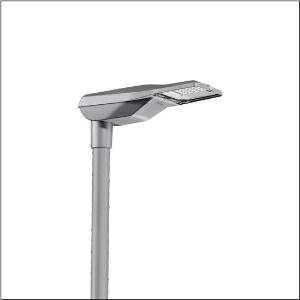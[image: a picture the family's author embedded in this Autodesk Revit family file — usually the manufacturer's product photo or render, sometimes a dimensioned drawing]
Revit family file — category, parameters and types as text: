
# Revit family: streetlight_sl_21_iq_micro___st1_0a_5xe1d41d08cb_ed56
name_source: partatom
category: Lighting Fixtures
units: mm (PartAtom-declared; Revit-internal decimal feet)

## family parameters
Cut with Voids When Loaded = No
Host = Face
Light Source = No
Part Type = Normal
Room Calculation Point = No
Round Connector Dimension = Use Diameter
Shared = No

## types (1)
- --- (1 x LED, 2980 lm, 19.4 W, 4000K)
    Apparent Load = 19 VA
    CIE Flux Codes = 37 72 97 100 100
    Color Rendering = 70
    Color Temperature = 4000K
    Default Elevation = 1800 mm
    Description = Streetlight SL 21 iQ micro, mast luminaire, primary light control with lens, of PMMA, primary optical cover: cover, of toughened safety glass, transparent, light distribution: ST1.0a, light emission: direct distribution, primary light characteristic: asymmetric, installation type: post-top, side-entry, LED, High Power LED, rated luminous flux: 2.980lm, luminous efficacy: 154lm/W, light colour: 740, colour temperature: 4000K, control gear: iQ-Comfort, control: Auto-Match, Temp-Guard, Lumen-Switch, Night-Set, Smart-Wire, Light-Fading, Desk-Remote (wireless, voltage-free reading and setting of iQ features in the workshop via application-optimized NFC function/RFID function), optimised constant luminous flux control (CLO 2.0), pre-setting: linear dimming characteristic, mains connection: 220..240V, AC, 50/60Hz, start of lifetime: 19W, end of service life: 20W, reduction: 10W, luminaire housing, of diecast aluminium, powder-coated, SITECO metallic grey (DB 702S), corrosivity category C5 high according to DIN EN ISO 12944, please order mast flange separately, inclination adjustable: 0°, 5°, 10°, 15°, sealing non-destructively replaceable, multi-level sealing system, length: 528mm, width: 235mm, height: 110mm, mast flange for spigot size: 42mm (side-entry): 5XC10008XM4, 60/48mm (side-entry/post-top): 5XC10108XM2, 76/60mm (side-entry/post-top): 5XC10108XM1, protection rating (complete): IP66, insulation class (complete): insulation class II (safety insulation), certification: CE, ENEC, ENEC+, VDE, impact resistance: IK10, permissible operating ambient temperature for outdoor applications: -40..+50°C, standard-compliant lighting for roads and squares, packaging unit: 1 piece

Light Distribution: ST1.0a
    Height = 110 mm
    Lamp = 1 x LED
    Lamp Light Flux = 2980 lm
    Lamp Power = 19.4 W
    Lamp count = 1
    Length = 528 mm
    Luminous efficacy = 154 lm/W
    Manufacturer = Siteco
    ModVariant = No
    Model = 5XE1D41D08CB
    Mounting Place = Pole
    Mounting Type = Pole top
    Number of Poles = 1
    OnlyDefault = Yes
    Power Factor = 1
    Product Name = Streetlight SL 21 iQ micro | ST1.0a
    Product group = mast luminaire | pylon top
    ProductGroupID = 6100
    Protection Class = Protection class II
    Protection Degree = IP 66
    RLX_Detail_Level = 1
    RLX_Emergency_Light_Flux = 0 lm
    RLX_Emergency_Type = 0
    RLX_Emergency_Type_DB = No
    RlxData = <blob elided: 98889 chars, md5=e276a93e>
    Socket = socket
    Standby Power = 0 W
    System Light Flux = 2980 lm
    System Power = 19 W
    Type Comments = factory setting: luminous flux: 100 % | dim-lin: 254 | 387 mA
    Type Image = l_1006881.jpg
    URL = http://relux.com
    VarID = @adj_140267
    Voltage = 0 V
    Weight = 0.00 kg
    Width = 235 mm

## geometry (parser evidence)
native form markers: Blend x4, Sweep x12
no freeform markers — native parametric forms only
